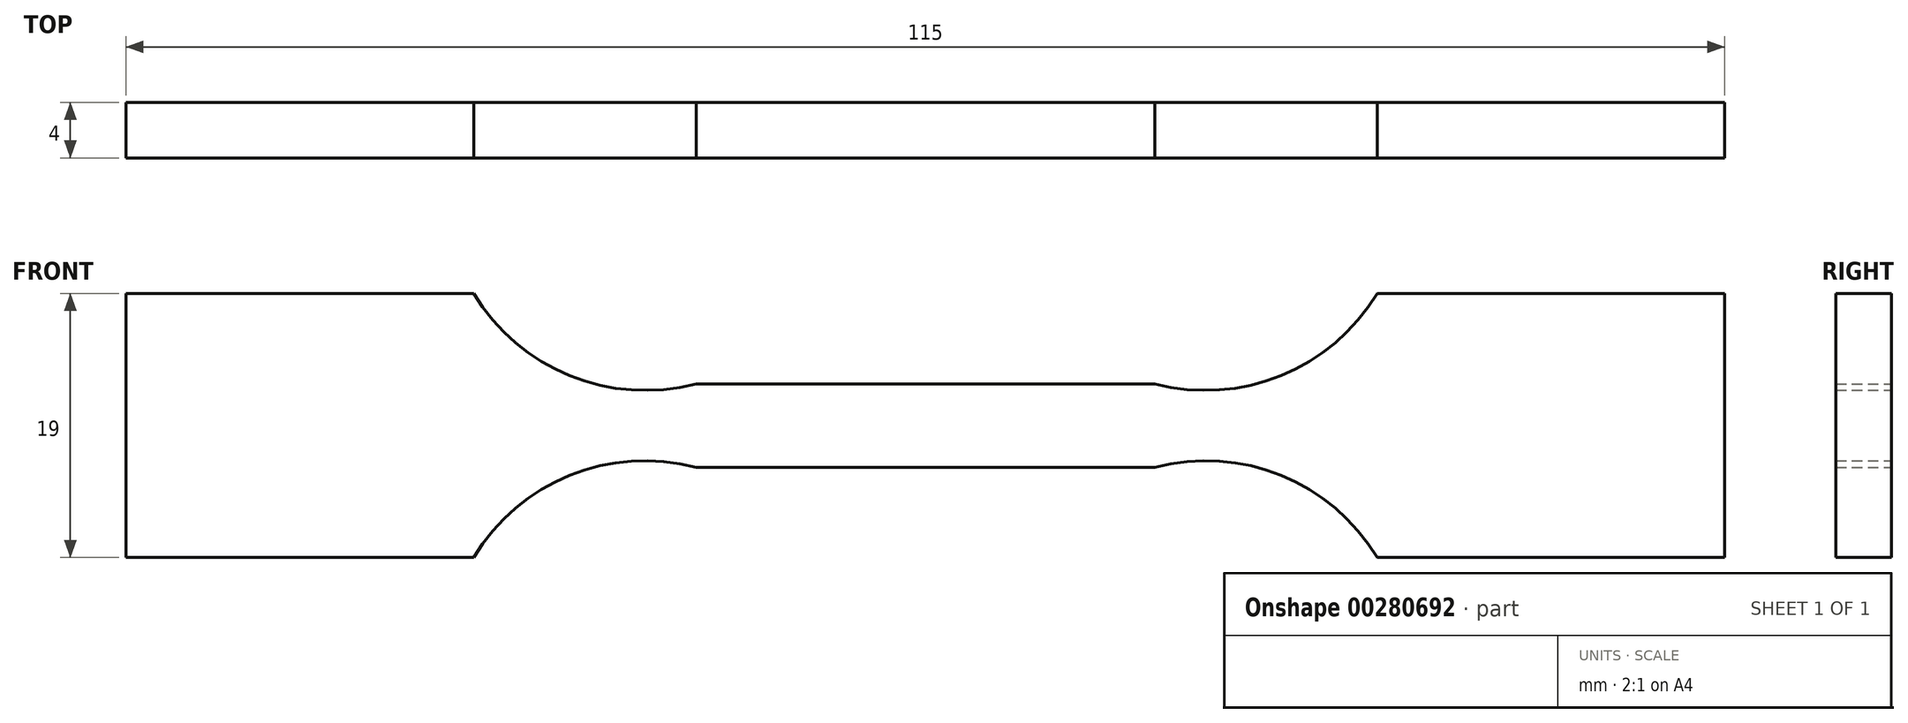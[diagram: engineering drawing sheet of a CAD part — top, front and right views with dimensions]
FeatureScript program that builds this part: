
annotation { "Feature Type Name" : "Feature", "Feature Type Description" : "" }
export const myFeature = defineFeature(function(context is Context, id is Id, definition is map)
    precondition{}
    {
        {
            var Q0;
            Q0=qCreatedBy(makeId("Front.planeOp"),FACE);
            var sketch = newSketch(context, id + "F0", { "sketchPlane" : qUnion([Q0])});
            skLineSegment(sketch, "E0", {"start": v(0, 3) * mm, "end": v(16.5, 3) * mm});
            skArc(sketch, "E1", {"start": v(16.5, 3) * mm, "mid": v(25.58, 3.59) * mm, "end": v(32.5, 9.5) * mm});
            skLineSegment(sketch, "E2", {"start": v(32.5, 9.5) * mm, "end": v(57.5, 9.5) * mm});
            skLineSegment(sketch, "E3", {"start": v(57.5, 9.5) * mm, "end": v(57.5, 0) * mm});
            skLineSegment(sketch, "E4.MirrorCS", {"start": v(0, 3) * mm, "end": v(-16.5, 3) * mm});
            skLineSegment(sketch, "E5.MirrorCS", {"start": v(-57.5, 9.5) * mm, "end": v(-57.5, 0) * mm});
            skLineSegment(sketch, "E6.MirrorCS", {"start": v(-32.5, 9.5) * mm, "end": v(-57.5, 9.5) * mm});
            skArc(sketch, "E7.MirrorCS", {"start": v(-16.5, 3) * mm, "mid": v(-25.58, 3.59) * mm, "end": v(-32.5, 9.5) * mm});
            skLineSegment(sketch, "E8.MirrorCS", {"start": v(0, -3) * mm, "end": v(16.5, -3) * mm});
            skArc(sketch, "E9.MirrorCS", {"start": v(16.5, -3) * mm, "mid": v(25.58, -3.59) * mm, "end": v(32.5, -9.5) * mm});
            skLineSegment(sketch, "E10.MirrorCS", {"start": v(32.5, -9.5) * mm, "end": v(57.5, -9.5) * mm});
            skLineSegment(sketch, "E11.MirrorCS", {"start": v(57.5, -9.5) * mm, "end": v(57.5, 0) * mm});
            skLineSegment(sketch, "E12.MirrorCS", {"start": v(0, -3) * mm, "end": v(-16.5, -3) * mm});
            skArc(sketch, "E13.MirrorCS", {"start": v(-16.5, -3) * mm, "mid": v(-25.58, -3.59) * mm, "end": v(-32.5, -9.5) * mm});
            skLineSegment(sketch, "E14.MirrorCS", {"start": v(-32.5, -9.5) * mm, "end": v(-57.5, -9.5) * mm});
            skLineSegment(sketch, "E15.MirrorCS", {"start": v(-57.5, -9.5) * mm, "end": v(-57.5, 0) * mm});
            skSolve(sketch);
        }
        {
            var Q0;
            Q0 = qSketchRegion(id + "F0", true);
            extrude(context, id + "F1", {"entities" : qUnion([Q0]), "endBound" : BoundingType.SYMMETRIC, "depth" : 4 * mm});
        }
    });
